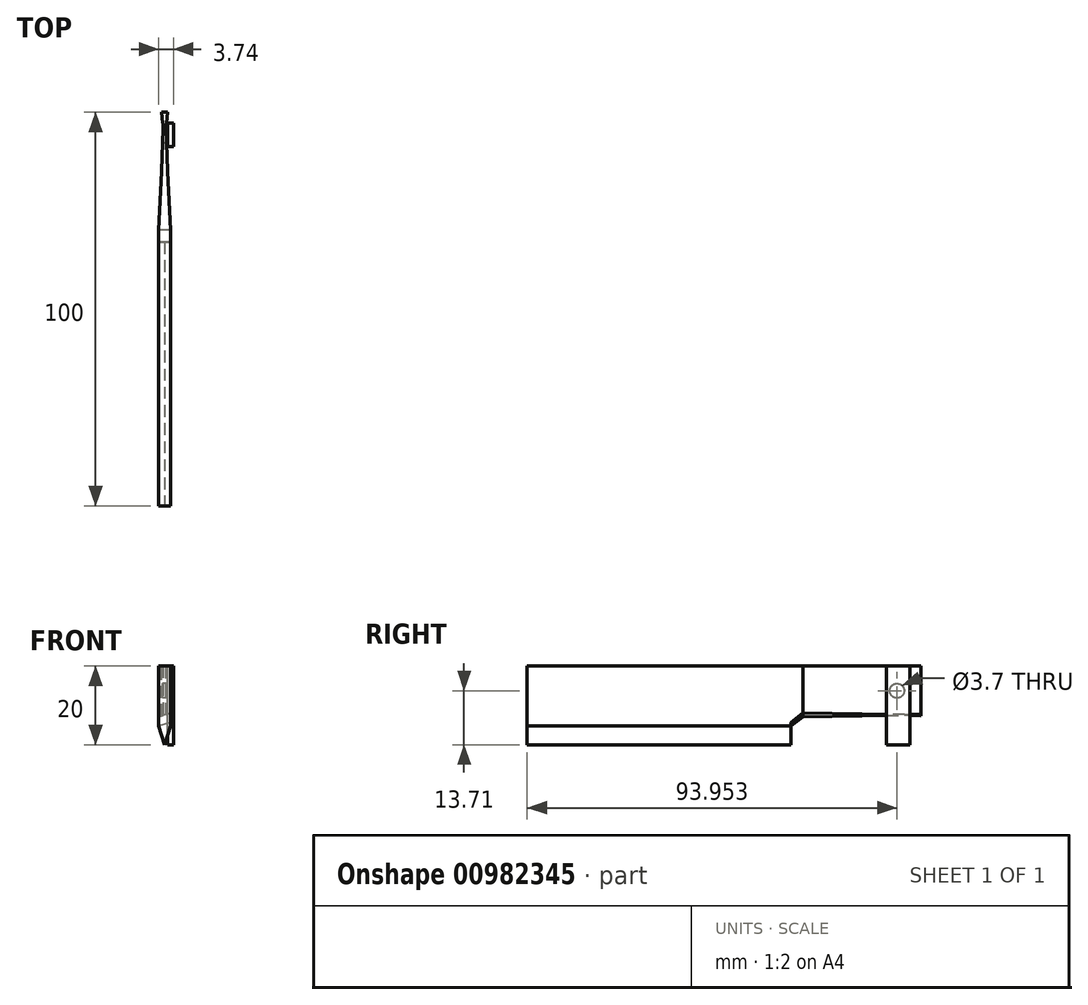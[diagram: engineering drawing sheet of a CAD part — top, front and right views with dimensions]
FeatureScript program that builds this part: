
annotation { "Feature Type Name" : "Feature", "Feature Type Description" : "" }
export const myFeature = defineFeature(function(context is Context, id is Id, definition is map)
    precondition{}
    {
        {
            var Q0;
            Q0=qCreatedBy(makeId("Top.planeOp"),FACE);
            var sketch = newSketch(context, id + "F0", { "sketchPlane" : qUnion([Q0])});
            skLineSegment(sketch, "E0.bottom", {"start": v(-1.5, 50) * mm, "end": v(1.5, 50) * mm});
            skLineSegment(sketch, "E0.top", {"start": v(-1.5, -50) * mm, "end": v(1.5, -50) * mm});
            skLineSegment(sketch, "E0.left", {"start": v(-1.5, 50) * mm, "end": v(-1.5, -50) * mm});
            skLineSegment(sketch, "E0.right", {"start": v(1.5, 50) * mm, "end": v(1.5, -50) * mm});
            skSolve(sketch);
        }
        {
            var Q0;
            Q0=makeQuery(id+"F0.imprint","IMPRINT",FACE,{"disambiguationData":[TD([[makeQuery(id+"F0.imprint","IMPRINT",EDGE,{"derivedFrom":sQuery(id+"F0.wireOp",EDGE,"E0.bottom")}),-1.0]])]});
            extrude(context, id + "F1", {"entities" : qUnion([Q0]), "depth" : 20 * mm, "offsetDistance" : 25 * mm});
        }
        {
            var Q0;
            Q0=makeQuery(id+"F1.opExtrude","SWEPT_FACE",FACE,{"disambiguationData":[OSD([sQuery(id+"F0.wireOp",EDGE,"E0.top")])]});
            var sketch = newSketch(context, id + "F2", { "sketchPlane" : qUnion([Q0])});
            skLineSegment(sketch, "E1", {"start": v(0, 0) * mm, "end": v(-1.5, 4.77) * mm});
            skLineSegment(sketch, "E2", {"start": v(0, 0) * mm, "end": v(1.5, 4.77) * mm});
            skLineSegment(sketch, "E3", {"start": v(-1.5, 4.77) * mm, "end": v(-2.5, 4.77) * mm});
            skLineSegment(sketch, "E4", {"start": v(-2.5, 4.77) * mm, "end": v(-2.5, 0) * mm});
            skLineSegment(sketch, "E5", {"start": v(-2.5, 0) * mm, "end": v(0, 0) * mm});
            skLineSegment(sketch, "E6", {"start": v(2.5, 0) * mm, "end": v(2.5, 4.77) * mm});
            skLineSegment(sketch, "E7", {"start": v(2.5, 4.77) * mm, "end": v(1.5, 4.77) * mm});
            skLineSegment(sketch, "E8", {"start": v(0, 0) * mm, "end": v(2.5, 0) * mm});
            skSolve(sketch);
        }
        {
            var Q0;
            {var subQ0=sQuery(id+"F2.wireOp",EDGE,"E3");Q0=makeQuery(id+"F2.imprint","IMPRINT",FACE,{"disambiguationData":[TD([[makeQuery(id+"F2.imprint","IMPRINT",EDGE,{"derivedFrom":subQ0}),1.0]])]});}
            var Q1;
            {var subQ0=sQuery(id+"F2.wireOp",EDGE,"E1");Q1=makeQuery(id+"F2.imprint","IMPRINT",FACE,{"disambiguationData":[TD([[makeQuery(id+"F2.imprint","IMPRINT",EDGE,{"derivedFrom":subQ0}),1.0]])]});}
            var Q2;
            {var subQ0=sQuery(id+"F2.wireOp",EDGE,"E2");Q2=makeQuery(id+"F2.imprint","IMPRINT",FACE,{"disambiguationData":[TD([[makeQuery(id+"F2.imprint","IMPRINT",EDGE,{"derivedFrom":subQ0}),-1.0]])]});}
            var Q3;
            {var subQ0=sQuery(id+"F2.wireOp",EDGE,"E6");Q3=makeQuery(id+"F2.imprint","IMPRINT",FACE,{"disambiguationData":[TD([[makeQuery(id+"F2.imprint","IMPRINT",EDGE,{"derivedFrom":subQ0}),1.0]])]});}
            extrude(context, id + "F3", {"entities" : qUnion([Q0, Q1, Q2, Q3]), "operationType" : NewBodyOperationType.REMOVE, "endBound" : BoundingType.THROUGH_ALL, "oppositeDirection" : true, "depth" : 25 * mm, "offsetDistance" : 25 * mm});
        }
        {
            var Q0;
            Q0=makeQuery(id+"F1.opExtrude","CAP_FACE",FACE,{"disambiguationData":[OSD([sQuery(id+"F0.wireOp",EDGE,"E0.bottom"),sQuery(id+"F0.wireOp",EDGE,"E0.top"),sQuery(id+"F0.wireOp",EDGE,"E0.left"),sQuery(id+"F0.wireOp",EDGE,"E0.right")])],"isStart":false});
            var sketch = newSketch(context, id + "F4", { "sketchPlane" : qUnion([Q0])});
            skLineSegment(sketch, "E9", {"start": v(-1.5, 20) * mm, "end": v(-1.62, 20) * mm});
            skLineSegment(sketch, "E10", {"start": v(-1.62, 20) * mm, "end": v(-1.62, 50) * mm});
            skLineSegment(sketch, "E11", {"start": v(1.62, 50) * mm, "end": v(1.62, 20) * mm});
            skLineSegment(sketch, "E12", {"start": v(1.62, 20) * mm, "end": v(1.5, 20) * mm});
            skLineSegment(sketch, "E13", {"start": v(0.75, 50) * mm, "end": v(1.62, 50) * mm});
            skLineSegment(sketch, "E14", {"start": v(-1.62, 50) * mm, "end": v(-0.75, 50) * mm});
            skLineSegment(sketch, "E15", {"start": v(0, 35) * mm, "end": v(-1.5, 35) * mm, "construction": true});
            skLineSegment(sketch, "E16", {"start": v(0, 35) * mm, "end": v(1.5, 35) * mm, "construction": true});
            skLineSegment(sketch, "E17", {"start": v(-1.5, 20) * mm, "end": v(-0.75, 35) * mm});
            skLineSegment(sketch, "E18", {"start": v(-1.5, 46.6) * mm, "end": v(1.5, 46.6) * mm, "construction": true});
            skLineSegment(sketch, "E19", {"start": v(-0.75, 35) * mm, "end": v(-0.38, 46.6) * mm});
            skLineSegment(sketch, "E20", {"start": v(-0.38, 46.6) * mm, "end": v(-0.75, 50) * mm});
            skLineSegment(sketch, "E21", {"start": v(0.38, 46.6) * mm, "end": v(0.75, 35) * mm});
            skLineSegment(sketch, "E22", {"start": v(0.75, 35) * mm, "end": v(1.5, 20) * mm});
            skLineSegment(sketch, "E23", {"start": v(0.38, 46.6) * mm, "end": v(0.75, 50) * mm});
            skSolve(sketch);
        }
        {
            var Q0;
            Q0 = qSketchRegion(id + "F4", true);
            extrude(context, id + "F5", {"entities" : qUnion([Q0]), "operationType" : NewBodyOperationType.REMOVE, "endBound" : BoundingType.THROUGH_ALL, "oppositeDirection" : true, "depth" : 25 * mm, "offsetDistance" : 25 * mm});
        }
        {
            var Q0;
            Q0=makeQuery(id+"F3.boolean.opBoolean","COPY",FACE,{"derivedFrom":makeQuery(id+"F3.opExtrude","SWEPT_FACE",FACE,{"disambiguationData":[OSD([sQuery(id+"F2.wireOp",EDGE,"E1")])]})});
            var sketch = newSketch(context, id + "F6", { "sketchPlane" : qUnion([Q0])});
            skLineSegment(sketch, "E24", {"start": v(-50.6, 7.22) * mm, "end": v(-20, 7.22) * mm});
            skLineSegment(sketch, "E25", {"start": v(-20, 7.22) * mm, "end": v(-17, 5) * mm});
            skLineSegment(sketch, "E26", {"start": v(-17, 5) * mm, "end": v(-17, -0.63) * mm});
            skLineSegment(sketch, "E27", {"start": v(-17, -0.63) * mm, "end": v(-50.6, -0.63) * mm});
            skLineSegment(sketch, "E28", {"start": v(-50.6, -0.63) * mm, "end": v(-50.6, 7.22) * mm});
            skSolve(sketch);
        }
        {
            var Q0;
            Q0 = qSketchRegion(id + "F6", true);
            extrude(context, id + "F7", {"entities" : qUnion([Q0]), "operationType" : NewBodyOperationType.REMOVE, "endBound" : BoundingType.THROUGH_ALL, "oppositeDirection" : true, "depth" : 25 * mm, "offsetDistance" : 25 * mm});
        }
        {
            var Q0;
            Q0=makeQuery(id+"F5.boolean.opBoolean","COPY",EDGE,{"derivedFrom":makeQuery(id+"F5.opExtrude","SWEPT_EDGE",EDGE,{"disambiguationData":[OSD([sQuery(id+"F4.wireOp",EDGE,"E17"),sQuery(id+"F4.wireOp",EDGE,"E19")])]})});
            var Q1;
            Q1=makeQuery(id+"F5.boolean.opBoolean","COPY",EDGE,{"derivedFrom":makeQuery(id+"F5.opExtrude","SWEPT_EDGE",EDGE,{"disambiguationData":[OSD([sQuery(id+"F4.wireOp",EDGE,"E21"),sQuery(id+"F4.wireOp",EDGE,"E22")])]})});
            var Q2;
            Q2=makeQuery(id+"F5.boolean.opBoolean","COPY",EDGE,{"derivedFrom":makeQuery(id+"F5.opExtrude","SWEPT_EDGE",EDGE,{"disambiguationData":[OSD([sQuery(id+"F4.wireOp",EDGE,"E21"),sQuery(id+"F4.wireOp",EDGE,"E23")])]})});
            var Q3;
            Q3=makeQuery(id+"F5.boolean.opBoolean","COPY",EDGE,{"derivedFrom":makeQuery(id+"F5.opExtrude","SWEPT_EDGE",EDGE,{"disambiguationData":[OSD([sQuery(id+"F4.wireOp",EDGE,"E19"),sQuery(id+"F4.wireOp",EDGE,"E20")])]})});
            fillet(context, id + "F8", {"entities" : qUnion([Q0, Q1, Q2, Q3]), "radius" : 10 * mm, "tangentPropagation" : true, "allowEdgeOverflow" : false});
        }
        {
            var Q0;
            Q0=makeQuery(id+"F5.boolean.opBoolean","COPY",FACE,{"derivedFrom":makeQuery(id+"F5.opExtrude","SWEPT_FACE",FACE,{"disambiguationData":[OSD([sQuery(id+"F4.wireOp",EDGE,"E19")])]})});
            var sketch = newSketch(context, id + "F9", { "sketchPlane" : qUnion([Q0])});
            skLineSegment(sketch, "E29", {"start": v(-43.93, 20) * mm, "end": v(-43.93, 7.42) * mm, "construction": true});
            skCircle(sketch, "E30", {"center": v(-43.93, 13.71) * mm, "radius": 1.85 * mm});
            skSolve(sketch);
        }
        {
            var Q0;
            Q0=makeQuery(id+"F9.imprint","IMPRINT",FACE,{"disambiguationData":[TD([[makeQuery(id+"F9.imprint","IMPRINT",EDGE,{"derivedFrom":sQuery(id+"F9.wireOp",EDGE,"E30")}),1.0]])]});
            var Q1;
            Q1=sQuery(id+"F9.wireOp",EDGE,"E30");
            extrude(context, id + "F10", {"entities" : qUnion([Q0]), "operationType" : NewBodyOperationType.REMOVE, "surfaceEntities" : qUnion([Q1]), "endBound" : BoundingType.THROUGH_ALL, "oppositeDirection" : true, "depth" : 25 * mm, "offsetDistance" : 25 * mm});
        }
        {
            var Q0;
            Q0=makeQuery(id+"F1.opExtrude","CAP_FACE",FACE,{"disambiguationData":[OSD([sQuery(id+"F0.wireOp",EDGE,"E0.bottom"),sQuery(id+"F0.wireOp",EDGE,"E0.top"),sQuery(id+"F0.wireOp",EDGE,"E0.left"),sQuery(id+"F0.wireOp",EDGE,"E0.right")])],"isStart":false});
            var sketch = newSketch(context, id + "F11", { "sketchPlane" : qUnion([Q0])});
            skLineSegment(sketch, "E31.bottom", {"start": v(0.74, 47.3) * mm, "end": v(2.24, 47.3) * mm, "construction": true});
            skLineSegment(sketch, "E31.top", {"start": v(0.74, 41.27) * mm, "end": v(2.24, 41.27) * mm});
            skLineSegment(sketch, "E32.bottom", {"start": v(0.74, 47.3) * mm, "end": v(2.24, 47.3) * mm});
            skLineSegment(sketch, "E32.top", {"start": v(0.74, 41.27) * mm, "end": v(2.24, 41.27) * mm, "construction": true});
            skLineSegment(sketch, "E33", {"start": v(0.74, 47.3) * mm, "end": v(0.74, 41.27) * mm});
            skLineSegment(sketch, "E34", {"start": v(2.24, 47.3) * mm, "end": v(2.24, 41.27) * mm});
            skSolve(sketch);
        }
        {
            var Q0;
            Q0=makeQuery(id+"F11.imprint","IMPRINT",FACE,{"disambiguationData":[TD([[makeQuery(id+"F11.imprint","IMPRINT",EDGE,{"derivedFrom":sQuery(id+"F11.wireOp",EDGE,"E31.top")}),1.0]])]});
            extrude(context, id + "F12", {"entities" : qUnion([Q0]), "oppositeDirection" : true, "depth" : 20 * mm, "offsetDistance" : 25 * mm});
        }
        {
            var Q0;
            Q0=sQuery(id+"F9.wireOp",EDGE,"E30");
            extrude(context, id + "F13", {"bodyType" : ToolBodyType.SURFACE, "surfaceEntities" : qUnion([Q0]), "oppositeDirection" : true, "depth" : 4 * mm, "offsetDistance" : 25 * mm});
        }
    });
